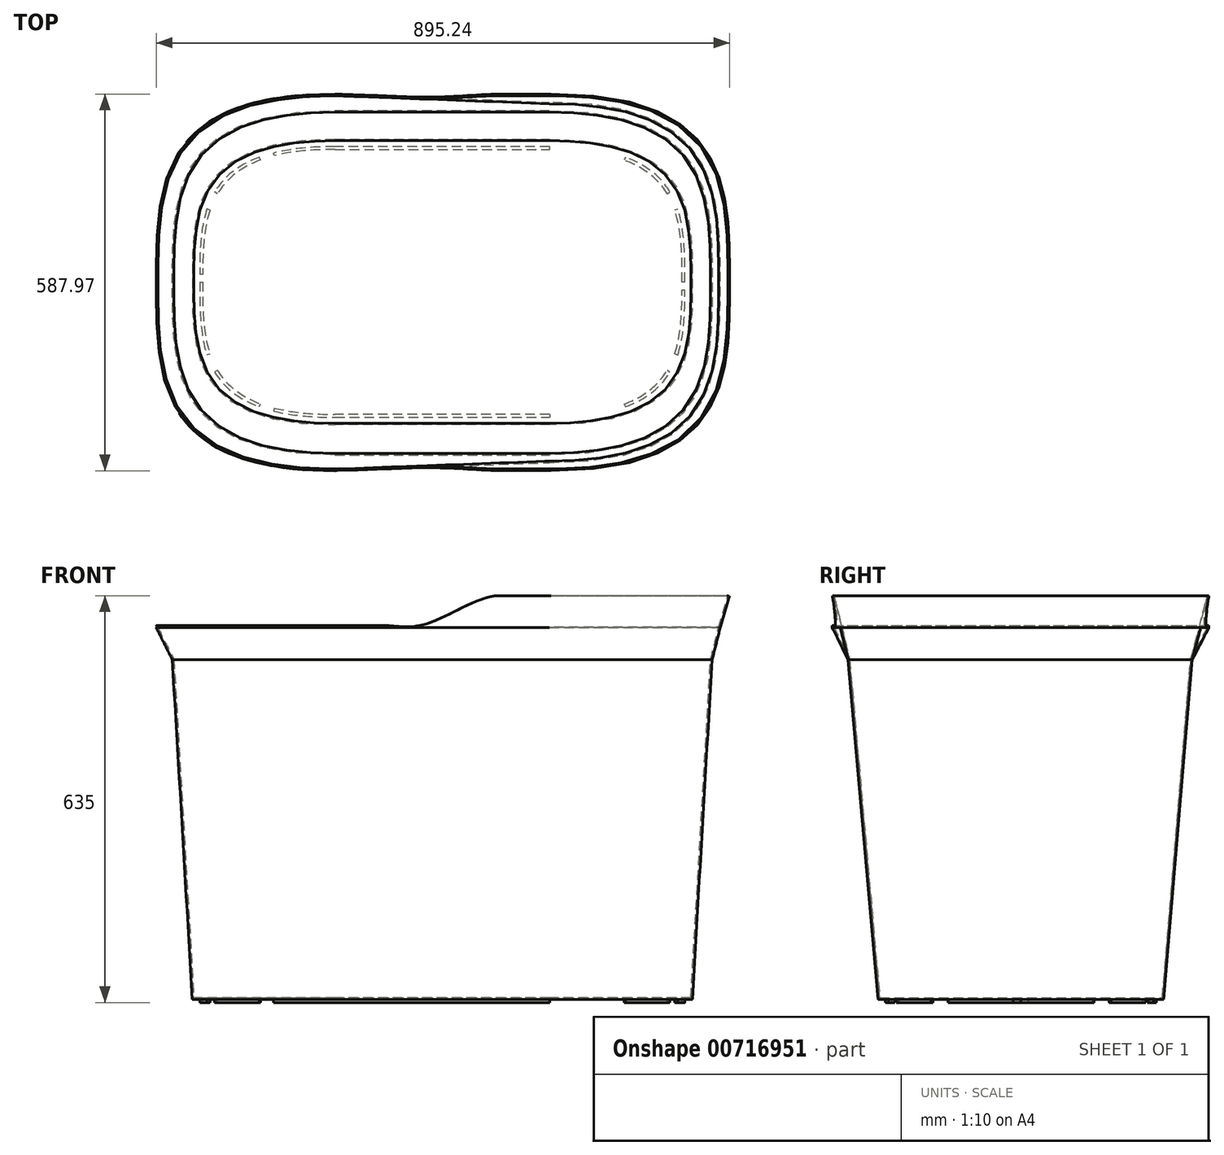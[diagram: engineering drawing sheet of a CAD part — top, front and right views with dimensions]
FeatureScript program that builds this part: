
annotation { "Feature Type Name" : "Feature", "Feature Type Description" : "" }
export const myFeature = defineFeature(function(context is Context, id is Id, definition is map)
    precondition{}
    {
        {
            var Q0;
            Q0=qCreatedBy(makeId("Top.planeOp"),FACE);
            cPlane(context, id + "F0", {"entities" : qUnion([Q0]), "cplaneType" : CPlaneType.OFFSET, "offset" : 530 * mm, "width" : 150 * mm, "height" : 150 * mm});
        }
        {
            var Q0;
            Q0=qCreatedBy(makeId("Top.planeOp"),FACE);
            var sketch = newSketch(context, id + "F1", { "sketchPlane" : qUnion([Q0])});
            skFitSpline(sketch, "E0", {"points": [v(557.64, 0) * mm, v(780.43, -222.79) * mm, v(557.64, -445.57) * mm], "startDerivative": vector(1336.72, 0) * mm, "endDerivative": vector(-1336.72, 0) * mm});
            skFitSpline(sketch, "E1", {"points": [v(222.79, 0) * mm, v(0, -222.79) * mm, v(222.79, -445.57) * mm], "startDerivative": vector(-1336.72, 0) * mm, "endDerivative": vector(1336.72, 0) * mm});
            skLineSegment(sketch, "E2", {"start": v(222.79, 0) * mm, "end": v(557.64, 0) * mm});
            skLineSegment(sketch, "E3", {"start": v(557.64, -445.57) * mm, "end": v(222.79, -445.57) * mm});
            skSolve(sketch);
        }
        {
            var Q0;
            Q0=qCreatedBy(id+"F0.planeOp",FACE);
            var sketch = newSketch(context, id + "F2", { "sketchPlane" : qUnion([Q0])});
            skFitSpline(sketch, "E4", {"points": [v(557.43, 44.62) * mm, v(811.28, -224) * mm, v(557.43, -492.62) * mm], "startDerivative": vector(1523.1, 0) * mm, "endDerivative": vector(-1523.1, 0) * mm});
            skFitSpline(sketch, "E5", {"points": [v(222.57, -492.62) * mm, v(-31.28, -224) * mm, v(222.57, 44.62) * mm], "startDerivative": vector(-1523.1, 0) * mm, "endDerivative": vector(1523.1, 0) * mm});
            skLineSegment(sketch, "E6", {"start": v(557.43, 44.62) * mm, "end": v(222.57, 44.62) * mm});
            skLineSegment(sketch, "E7", {"start": v(222.57, -492.62) * mm, "end": v(557.43, -492.62) * mm});
            skSolve(sketch);
        }
        {
            var Q0;
            Q0=makeQuery(id+"F1.imprint","IMPRINT",FACE,{"disambiguationData":[TD([[makeQuery(id+"F1.imprint","IMPRINT",EDGE,{"derivedFrom":sQuery(id+"F1.wireOp",EDGE,"E0")}),-1.0]])]});
            var Q1;
            Q1=makeQuery(id+"F2.imprint","IMPRINT",FACE,{"disambiguationData":[TD([[makeQuery(id+"F2.imprint","IMPRINT",EDGE,{"derivedFrom":sQuery(id+"F2.wireOp",EDGE,"E4")}),-1.0]])]});
            loft(context, id + "F3", {"sheetProfilesArray" : [{ "sheetProfileEntities" : qUnion([Q0]) }, { "sheetProfileEntities" : qUnion([Q1]) }]});
        }
        {
            var Q0;
            Q0=qCreatedBy(id+"F0.planeOp",FACE);
            cPlane(context, id + "F4", {"entities" : qUnion([Q0]), "cplaneType" : CPlaneType.OFFSET, "offset" : 50 * mm, "width" : 150 * mm, "height" : 150 * mm});
        }
        {
            var Q0;
            Q0=qCreatedBy(id+"F4.planeOp",FACE);
            cPlane(context, id + "F5", {"entities" : qUnion([Q0]), "cplaneType" : CPlaneType.OFFSET, "offset" : 50 * mm, "width" : 150 * mm, "height" : 150 * mm});
        }
        {
            var Q0;
            Q0=qCreatedBy(id+"F4.planeOp",FACE);
            var sketch = newSketch(context, id + "F6", { "sketchPlane" : qUnion([Q0])});
            skFitSpline(sketch, "E8", {"points": [v(222.7, 70.47) * mm, v(-56.44, -223.44) * mm, v(222.7, -517.35) * mm], "startDerivative": vector(-1674.87, 0) * mm, "endDerivative": vector(1674.87, 0) * mm});
            skFitSpline(sketch, "E9", {"points": [v(557.56, -504.67) * mm, v(824.02, -223.44) * mm, v(557.56, 57.78) * mm], "startDerivative": vector(1598.75, 0) * mm, "endDerivative": vector(-1598.75, 0) * mm});
            skLineSegment(sketch, "E10", {"start": v(222.7, 70.47) * mm, "end": v(557.56, 57.78) * mm});
            skLineSegment(sketch, "E11", {"start": v(222.7, -517.35) * mm, "end": v(557.56, -504.67) * mm});
            skSolve(sketch);
        }
        {
            var Q1;
            Q1=makeQuery(id+"F6.imprint","IMPRINT",FACE,{"disambiguationData":[TD([[makeQuery(id+"F6.imprint","IMPRINT",EDGE,{"derivedFrom":sQuery(id+"F6.wireOp",EDGE,"E8")}),1.0]])]});
            var Q2;
            Q2=makeQuery(id+"F3.opLoft","CAP_FACE",FACE,{"disambiguationData":[OSD([makeQuery(id+"F2.imprint","IMPRINT",FACE,{"disambiguationData":[TD([[makeQuery(id+"F2.imprint","IMPRINT",EDGE,{"derivedFrom":sQuery(id+"F2.wireOp",EDGE,"E4")}),-1.0]])]})])],"isStart":true});
            loft(context, id + "F7", {"operationType" : NewBodyOperationType.ADD, "sheetProfilesArray" : [{ "sheetProfileEntities" : qUnion([Q1]) }, { "sheetProfileEntities" : qUnion([Q2]) }]});
        }
        {
            var Q0;
            Q0=qCreatedBy(id+"F5.planeOp",FACE);
            var sketch = newSketch(context, id + "F8", { "sketchPlane" : qUnion([Q0])});
            skFitSpline(sketch, "E12", {"points": [v(222.62, 70.62) * mm, v(-56.53, -223.3) * mm, v(222.62, -517.2) * mm], "startDerivative": vector(-1674.87, 0) * mm, "endDerivative": vector(1674.87, 0) * mm});
            skFitSpline(sketch, "E13", {"points": [v(559.65, -517.2) * mm, v(838.8, -223.3) * mm, v(559.65, 70.62) * mm], "startDerivative": vector(1674.87, 0) * mm, "endDerivative": vector(-1674.87, 0) * mm});
            skLineSegment(sketch, "E14", {"start": v(222.62, 70.62) * mm, "end": v(559.65, 70.62) * mm});
            skLineSegment(sketch, "E15", {"start": v(559.65, -517.2) * mm, "end": v(222.62, -517.2) * mm});
            skSolve(sketch);
        }
        {
            var Q1;
            Q1=makeQuery(id+"F7.opLoft","CAP_FACE",FACE,{"disambiguationData":[OSD([makeQuery(id+"F6.imprint","IMPRINT",FACE,{"disambiguationData":[TD([[makeQuery(id+"F6.imprint","IMPRINT",EDGE,{"derivedFrom":sQuery(id+"F6.wireOp",EDGE,"E8")}),1.0]])]})])],"isStart":true});
            var Q2;
            Q2=makeQuery(id+"F8.imprint","IMPRINT",FACE,{"disambiguationData":[TD([[makeQuery(id+"F8.imprint","IMPRINT",EDGE,{"derivedFrom":sQuery(id+"F8.wireOp",EDGE,"E12")}),1.0]])]});
            loft(context, id + "F9", {"operationType" : NewBodyOperationType.ADD, "sheetProfilesArray" : [{ "sheetProfileEntities" : qUnion([Q1]) }, { "sheetProfileEntities" : qUnion([Q2]) }]});
        }
        {
            var Q0;
            Q0=makeQuery(id+"F9.opLoft","CAP_FACE",FACE,{"disambiguationData":[OSD([makeQuery(id+"F8.imprint","IMPRINT",FACE,{"disambiguationData":[TD([[makeQuery(id+"F8.imprint","IMPRINT",EDGE,{"derivedFrom":sQuery(id+"F8.wireOp",EDGE,"E12")}),1.0]])]})])],"isStart":true});
            shell(context, id + "F10", {"entities" : qUnion([Q0]), "thickness" : 2.5 * mm});
        }
        {
            var Q0;
            Q0=qCreatedBy(makeId("Front.planeOp"),FACE);
            cPlane(context, id + "F11", {"entities" : qUnion([Q0]), "cplaneType" : CPlaneType.OFFSET, "offset" : 200 * mm, "oppositeDirection" : true, "width" : 150 * mm, "height" : 150 * mm});
        }
        {
            var Q0;
            Q0=qCreatedBy(id+"F11.planeOp",FACE);
            var sketch = newSketch(context, id + "F12", { "sketchPlane" : qUnion([Q0])});
            skLineSegment(sketch, "E16", {"start": v(-86.66, 583.35) * mm, "end": v(303.25, 583.35) * mm});
            skFitSpline(sketch, "E17", {"points": [v(303.25, 583.35) * mm, v(354.53, 583.35) * mm, v(408.19, 604.82) * mm, v(466.61, 628.66) * mm, v(527.43, 631.05) * mm], "startDerivative": vector(219.65, -20.62) * mm, "endDerivative": vector(240.67, -11.34) * mm});
            skLineSegment(sketch, "E18", {"start": v(527.43, 631.05) * mm, "end": v(527.43, 657.28) * mm});
            skLineSegment(sketch, "E19", {"start": v(527.43, 657.28) * mm, "end": v(-89.05, 657.28) * mm});
            skLineSegment(sketch, "E20", {"start": v(-89.05, 657.28) * mm, "end": v(-86.66, 583.35) * mm});
            skSolve(sketch);
        }
        {
            var Q0;
            Q0=makeQuery(id+"F12.imprint","IMPRINT",FACE,{"disambiguationData":[TD([[makeQuery(id+"F12.imprint","IMPRINT",EDGE,{"derivedFrom":sQuery(id+"F12.wireOp",EDGE,"E16")}),1.0]])]});
            extrude(context, id + "F13", {"entities" : qUnion([Q0]), "depth" : 812 * mm, "offsetDistance" : 25 * mm});
        }
        {
            var Q0;
            Q0=makeQuery(id+"F13.opExtrude","SWEPT_BODY",BODY,{"disambiguationData":[OSD([sQuery(id+"F12.wireOp",EDGE,"E16"),sQuery(id+"F12.wireOp",EDGE,"E17"),sQuery(id+"F12.wireOp",EDGE,"E18"),sQuery(id+"F12.wireOp",EDGE,"E19"),sQuery(id+"F12.wireOp",EDGE,"E20")])]});
            var Q1;
            Q1=makeQuery(id+"F3.opLoft","SWEPT_BODY",BODY,{"disambiguationData":[OSD([makeQuery(id+"F1.imprint","IMPRINT",FACE,{"disambiguationData":[TD([[makeQuery(id+"F1.imprint","IMPRINT",EDGE,{"derivedFrom":sQuery(id+"F1.wireOp",EDGE,"E0")}),-1.0]])]}),makeQuery(id+"F2.imprint","IMPRINT",FACE,{"disambiguationData":[TD([[makeQuery(id+"F2.imprint","IMPRINT",EDGE,{"derivedFrom":sQuery(id+"F2.wireOp",EDGE,"E4")}),-1.0]])]})])]});
            booleanBodies(context, id + "F14", {"operationType" : BooleanOperationType.SUBTRACTION, "tools" : qUnion([Q0]), "targets" : qUnion([Q1])});
        }
        {
            var Q0;
            Q0=qCreatedBy(makeId("Top.planeOp"),FACE);
            var sketch = newSketch(context, id + "F15", { "sketchPlane" : qUnion([Q0])});
            skFitSpline(sketch, "E21", {"points": [v(222.77, -11.5) * mm, v(11.47, -222.8) * mm, v(222.77, -434.11) * mm], "startDerivative": vector(-1267.82, 0) * mm, "endDerivative": vector(1267.82, 0) * mm});
            skFitSpline(sketch, "E22", {"points": [v(557.63, -434.11) * mm, v(768.93, -222.8) * mm, v(557.63, -11.5) * mm], "startDerivative": vector(1267.82, 0) * mm, "endDerivative": vector(-1267.82, 0) * mm});
            skLineSegment(sketch, "E23", {"start": v(222.77, -434.11) * mm, "end": v(557.63, -434.11) * mm});
            skLineSegment(sketch, "E24", {"start": v(557.63, -11.5) * mm, "end": v(222.77, -11.5) * mm});
            skLineSegment(sketch, "E25", {"start": v(222.77, -434.11) * mm, "end": v(222.77, -429.56) * mm});
            skLineSegment(sketch, "E26", {"start": v(222.77, -11.5) * mm, "end": v(222.77, -16.06) * mm});
            skLineSegment(sketch, "E27", {"start": v(11.47, -222.8) * mm, "end": v(16.03, -222.8) * mm});
            skFitSpline(sketch, "E28", {"points": [v(222.77, -16.06) * mm, v(16.03, -222.8) * mm, v(222.77, -429.56) * mm], "startDerivative": vector(-1232.53, 6.72) * mm, "endDerivative": vector(1236.23, 0) * mm});
            skLineSegment(sketch, "E29", {"start": v(557.63, -429.56) * mm, "end": v(557.63, -434.11) * mm});
            skLineSegment(sketch, "E30", {"start": v(222.77, -16.06) * mm, "end": v(557.63, -16.06) * mm});
            skLineSegment(sketch, "E31", {"start": v(557.63, -16.06) * mm, "end": v(557.63, -11.5) * mm});
            skLineSegment(sketch, "E32", {"start": v(222.77, -16.06) * mm, "end": v(263.71, -16.06) * mm});
            skLineSegment(sketch, "E33", {"start": v(222.77, -11.5) * mm, "end": v(263.71, -11.5) * mm});
            skLineSegment(sketch, "E34", {"start": v(263.71, -11.5) * mm, "end": v(263.71, -16.06) * mm});
            skLineSegment(sketch, "E35", {"start": v(557.63, -16.06) * mm, "end": v(516.7, -16.06) * mm});
            skLineSegment(sketch, "E36", {"start": v(557.63, -11.5) * mm, "end": v(516.7, -11.5) * mm});
            skLineSegment(sketch, "E37", {"start": v(516.7, -11.5) * mm, "end": v(516.7, -16.06) * mm});
            skLineSegment(sketch, "E38", {"start": v(263.71, -16.06) * mm, "end": v(516.7, -16.06) * mm});
            skLineSegment(sketch, "E39", {"start": v(127.99, -25.7) * mm, "end": v(126.87, -21.43) * mm});
            skLineSegment(sketch, "E40", {"start": v(106.45, -32.33) * mm, "end": v(104.68, -28.13) * mm});
            skLineSegment(sketch, "E41", {"start": v(39.25, -85.18) * mm, "end": v(34.92, -82.21) * mm});
            skLineSegment(sketch, "E42", {"start": v(27.6, -110.77) * mm, "end": v(22.8, -108.93) * mm});
            skLineSegment(sketch, "E43", {"start": v(16.06, -210.69) * mm, "end": v(11.48, -210.69) * mm});
            skLineSegment(sketch, "E44", {"start": v(27.6, -335.43) * mm, "end": v(22.8, -336.69) * mm});
            skLineSegment(sketch, "E45", {"start": v(39.25, -360.6) * mm, "end": v(34.92, -363.4) * mm});
            skLineSegment(sketch, "E46", {"start": v(104.68, -417.48) * mm, "end": v(106.45, -412.93) * mm});
            skLineSegment(sketch, "E47", {"start": v(127.99, -419.57) * mm, "end": v(126.87, -424.19) * mm});
            skLineSegment(sketch, "E48", {"start": v(557.63, -11.5) * mm, "end": v(557.63, -16.06) * mm});
            skLineSegment(sketch, "E49", {"start": v(557.63, -434.11) * mm, "end": v(557.63, -429.56) * mm});
            skLineSegment(sketch, "E50", {"start": v(768.93, -222.8) * mm, "end": v(764.38, -222.8) * mm});
            skFitSpline(sketch, "E51", {"points": [v(557.63, -429.56) * mm, v(764.38, -222.8) * mm, v(557.63, -16.06) * mm], "startDerivative": vector(1232.53, -6.72) * mm, "endDerivative": vector(-1236.23, 0) * mm});
            skLineSegment(sketch, "E52", {"start": v(557.63, -429.56) * mm, "end": v(222.77, -429.56) * mm});
            skLineSegment(sketch, "E53", {"start": v(222.77, -429.56) * mm, "end": v(222.77, -434.11) * mm});
            skLineSegment(sketch, "E54", {"start": v(557.63, -429.56) * mm, "end": v(516.7, -429.56) * mm});
            skLineSegment(sketch, "E55", {"start": v(557.63, -434.11) * mm, "end": v(516.7, -434.11) * mm});
            skLineSegment(sketch, "E56", {"start": v(516.7, -434.11) * mm, "end": v(516.7, -429.56) * mm});
            skLineSegment(sketch, "E57", {"start": v(222.77, -429.56) * mm, "end": v(263.71, -429.56) * mm});
            skLineSegment(sketch, "E58", {"start": v(222.77, -434.11) * mm, "end": v(263.71, -434.11) * mm});
            skLineSegment(sketch, "E59", {"start": v(263.71, -434.11) * mm, "end": v(263.71, -429.56) * mm});
            skLineSegment(sketch, "E60", {"start": v(516.7, -429.56) * mm, "end": v(263.71, -429.56) * mm});
            skLineSegment(sketch, "E61", {"start": v(652.42, -419.92) * mm, "end": v(653.53, -424.19) * mm});
            skLineSegment(sketch, "E62", {"start": v(673.96, -413.3) * mm, "end": v(675.72, -417.48) * mm});
            skLineSegment(sketch, "E63", {"start": v(741.16, -360.44) * mm, "end": v(745.48, -363.4) * mm});
            skLineSegment(sketch, "E64", {"start": v(752.8, -334.85) * mm, "end": v(757.6, -336.69) * mm});
            skLineSegment(sketch, "E65", {"start": v(764.34, -234.93) * mm, "end": v(768.92, -234.93) * mm});
            skLineSegment(sketch, "E66", {"start": v(752.8, -110.18) * mm, "end": v(757.6, -108.93) * mm});
            skLineSegment(sketch, "E67", {"start": v(741.16, -85) * mm, "end": v(745.48, -82.21) * mm});
            skLineSegment(sketch, "E68", {"start": v(675.72, -28.13) * mm, "end": v(673.96, -32.68) * mm});
            skLineSegment(sketch, "E69", {"start": v(652.42, -26.05) * mm, "end": v(653.53, -21.43) * mm});
            skSolve(sketch);
        }
        {
            var Q0;
            Q0=makeQuery(id+"F15.imprint","IMPRINT",FACE,{"disambiguationData":[TD([[makeQuery(id+"F15.imprint","IMPRINT",EDGE,{"derivedFrom":sQuery(id+"F15.wireOp",EDGE,"E23")}),1.0]])]});
            var Q1;
            {var subQ0=sQuery(id+"F15.wireOp",EDGE,"E49");Q1=makeQuery(id+"F15.imprint","IMPRINT",FACE,{"disambiguationData":[TD([[makeQuery(id+"F15.imprint","IMPRINT",EDGE,{"derivedFrom":subQ0}),-1.0]])]});}
            var Q2;
            {var subQ0=sQuery(id+"F15.wireOp",EDGE,"E62");Q2=makeQuery(id+"F15.imprint","IMPRINT",FACE,{"disambiguationData":[TD([[makeQuery(id+"F15.imprint","IMPRINT",EDGE,{"derivedFrom":subQ0}),1.0]])]});}
            var Q3;
            {var subQ0=sQuery(id+"F15.wireOp",EDGE,"E64");Q3=makeQuery(id+"F15.imprint","IMPRINT",FACE,{"disambiguationData":[TD([[makeQuery(id+"F15.imprint","IMPRINT",EDGE,{"derivedFrom":subQ0}),1.0]])]});}
            var Q4;
            {var subQ0=sQuery(id+"F15.wireOp",EDGE,"E50");Q4=makeQuery(id+"F15.imprint","IMPRINT",FACE,{"disambiguationData":[TD([[makeQuery(id+"F15.imprint","IMPRINT",EDGE,{"derivedFrom":subQ0}),-1.0]])]});}
            var Q5;
            {var subQ0=sQuery(id+"F15.wireOp",EDGE,"E67");Q5=makeQuery(id+"F15.imprint","IMPRINT",FACE,{"disambiguationData":[TD([[makeQuery(id+"F15.imprint","IMPRINT",EDGE,{"derivedFrom":subQ0}),1.0]])]});}
            var Q6;
            {var subQ0=sQuery(id+"F15.wireOp",EDGE,"E48");Q6=makeQuery(id+"F15.imprint","IMPRINT",FACE,{"disambiguationData":[TD([[makeQuery(id+"F15.imprint","IMPRINT",EDGE,{"derivedFrom":subQ0}),1.0]])]});}
            var Q7;
            Q7=makeQuery(id+"F15.imprint","IMPRINT",FACE,{"disambiguationData":[TD([[makeQuery(id+"F15.imprint","IMPRINT",EDGE,{"derivedFrom":sQuery(id+"F15.wireOp",EDGE,"E24")}),1.0]])]});
            var Q8;
            {var subQ0=sQuery(id+"F15.wireOp",EDGE,"E26");Q8=makeQuery(id+"F15.imprint","IMPRINT",FACE,{"disambiguationData":[TD([[makeQuery(id+"F15.imprint","IMPRINT",EDGE,{"derivedFrom":subQ0}),-1.0]])]});}
            var Q9;
            {var subQ0=sQuery(id+"F15.wireOp",EDGE,"E40");Q9=makeQuery(id+"F15.imprint","IMPRINT",FACE,{"disambiguationData":[TD([[makeQuery(id+"F15.imprint","IMPRINT",EDGE,{"derivedFrom":subQ0}),1.0]])]});}
            var Q10;
            {var subQ0=sQuery(id+"F15.wireOp",EDGE,"E42");Q10=makeQuery(id+"F15.imprint","IMPRINT",FACE,{"disambiguationData":[TD([[makeQuery(id+"F15.imprint","IMPRINT",EDGE,{"derivedFrom":subQ0}),1.0]])]});}
            var Q11;
            {var subQ0=sQuery(id+"F15.wireOp",EDGE,"E27");Q11=makeQuery(id+"F15.imprint","IMPRINT",FACE,{"disambiguationData":[TD([[makeQuery(id+"F15.imprint","IMPRINT",EDGE,{"derivedFrom":subQ0}),-1.0]])]});}
            var Q12;
            {var subQ0=sQuery(id+"F15.wireOp",EDGE,"E45");Q12=makeQuery(id+"F15.imprint","IMPRINT",FACE,{"disambiguationData":[TD([[makeQuery(id+"F15.imprint","IMPRINT",EDGE,{"derivedFrom":subQ0}),1.0]])]});}
            var Q13;
            {var subQ2=sQuery(id+"F15.wireOp",EDGE,"E47");Q13=makeQuery(id+"F15.imprint","IMPRINT",FACE,{"disambiguationData":[TD([[makeQuery(id+"F15.imprint","IMPRINT",EDGE,{"derivedFrom":subQ2}),1.0]])]});}
            extrude(context, id + "F16", {"entities" : qUnion([Q0, Q1, Q2, Q3, Q4, Q5, Q6, Q7, Q8, Q9, Q10, Q11, Q12, Q13]), "operationType" : NewBodyOperationType.ADD, "oppositeDirection" : true, "depth" : 5 * mm, "offsetDistance" : 25 * mm});
        }
    });
